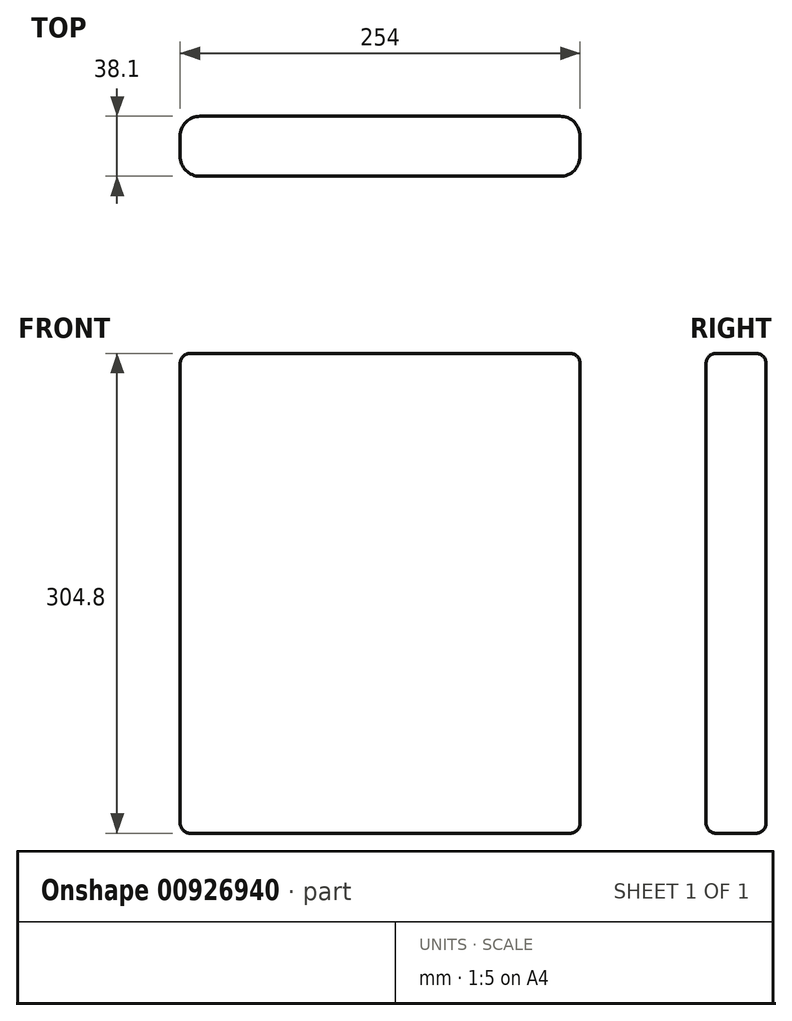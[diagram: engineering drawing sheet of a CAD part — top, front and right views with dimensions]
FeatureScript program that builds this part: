
annotation { "Feature Type Name" : "Feature", "Feature Type Description" : "" }
export const myFeature = defineFeature(function(context is Context, id is Id, definition is map)
    precondition{}
    {
        {
            var Q0;
            Q0=qCreatedBy(makeId("Front.planeOp"),FACE);
            var sketch = newSketch(context, id + "F0", { "sketchPlane" : qUnion([Q0])});
            skLineSegment(sketch, "E0", {"start": v(0, 0) * mm, "end": v(254, 0) * mm});
            skLineSegment(sketch, "E1", {"start": v(254, 0) * mm, "end": v(254, 304.8) * mm});
            skLineSegment(sketch, "E2", {"start": v(254, 304.8) * mm, "end": v(0, 304.8) * mm});
            skLineSegment(sketch, "E3", {"start": v(0, 304.8) * mm, "end": v(0, 0) * mm});
            skSolve(sketch);
        }
        {
            var Q0;
            Q0=makeQuery(id+"F0.imprint","IMPRINT",FACE,{"disambiguationData":[TD([[makeQuery(id+"F0.imprint","IMPRINT",EDGE,{"derivedFrom":sQuery(id+"F0.wireOp",EDGE,"E0")}),1.0]])]});
            extrude(context, id + "F1", {"entities" : qUnion([Q0]), "endBound" : BoundingType.SYMMETRIC, "depth" : 38.1 * mm, "offsetDistance" : 25.4 * mm});
        }
        {
            var Q0;
            Q0=makeQuery(id+"F1.opExtrude","CAP_EDGE",EDGE,{"disambiguationData":[OSD([sQuery(id+"F0.wireOp",EDGE,"E3")])],"isStart":false});
            var Q1;
            Q1=makeQuery(id+"F1.opExtrude","CAP_EDGE",EDGE,{"disambiguationData":[OSD([sQuery(id+"F0.wireOp",EDGE,"E1")])],"isStart":false});
            var Q2;
            Q2=makeQuery(id+"F1.opExtrude","CAP_EDGE",EDGE,{"disambiguationData":[OSD([sQuery(id+"F0.wireOp",EDGE,"E1")])],"isStart":true});
            var Q3;
            Q3=makeQuery(id+"F1.opExtrude","CAP_EDGE",EDGE,{"disambiguationData":[OSD([sQuery(id+"F0.wireOp",EDGE,"E3")])],"isStart":true});
            fillet(context, id + "F2", {"entities" : qUnion([Q0, Q1, Q2, Q3]), "radius" : 12.7 * mm, "tangentPropagation" : true, "allowEdgeOverflow" : false});
        }
        {
            var Q0;
            Q0=makeQuery(id+"F1.opExtrude","CAP_EDGE",EDGE,{"disambiguationData":[OSD([sQuery(id+"F0.wireOp",EDGE,"E2")])],"isStart":false});
            var Q1;
            Q1=makeQuery(id+"F1.opExtrude","CAP_EDGE",EDGE,{"disambiguationData":[OSD([sQuery(id+"F0.wireOp",EDGE,"E0")])],"isStart":false});
            fillet(context, id + "F3", {"entities" : qUnion([Q0, Q1]), "radius" : 6.35 * mm, "tangentPropagation" : true, "allowEdgeOverflow" : false});
        }
    });
